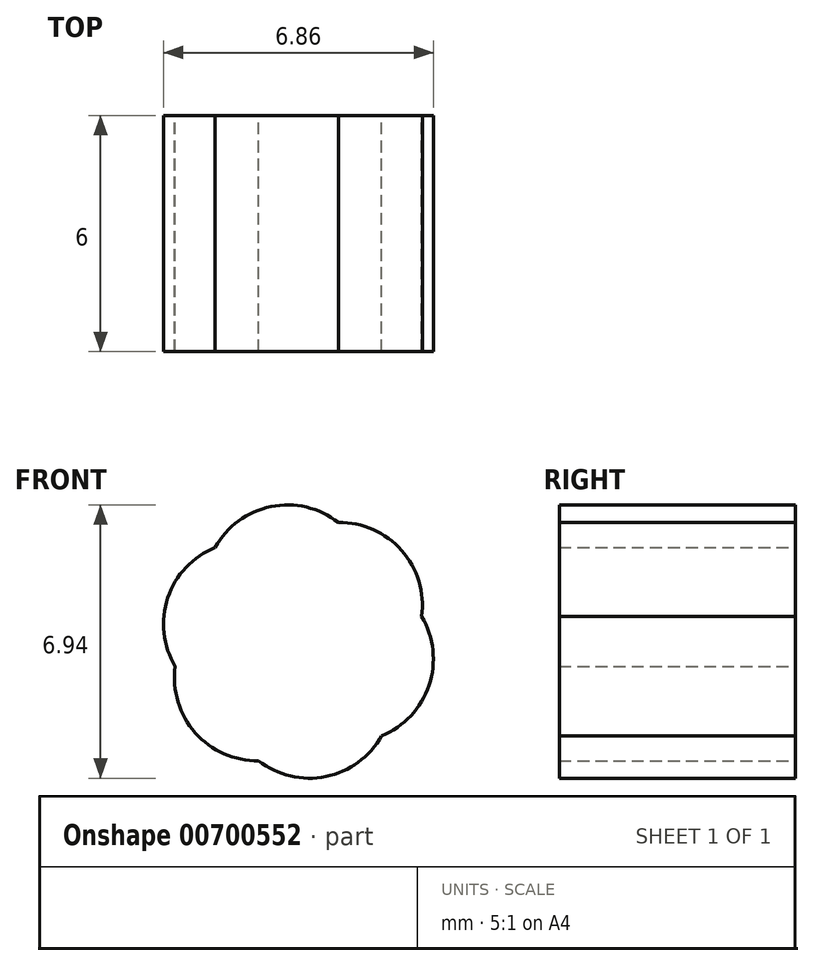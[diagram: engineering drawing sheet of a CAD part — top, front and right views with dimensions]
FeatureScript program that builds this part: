
annotation { "Feature Type Name" : "Feature", "Feature Type Description" : "" }
export const myFeature = defineFeature(function(context is Context, id is Id, definition is map)
    precondition{}
    {
        {
            var Q0;
            Q0=qCreatedBy(makeId("Front.planeOp"),FACE);
            var sketch = newSketch(context, id + "F0", { "sketchPlane" : qUnion([Q0])});
            skArc(sketch, "E0", {"start": v(3.13, 0.64) * mm, "mid": v(2.62, 2.32) * mm, "end": v(1.01, 3.03) * mm});
            skArc(sketch, "E1", {"start": v(2.11, -2.4) * mm, "mid": v(3.32, -1.11) * mm, "end": v(3.13, 0.64) * mm});
            skArc(sketch, "E2", {"start": v(-1.01, -3.03) * mm, "mid": v(0.7, -3.43) * mm, "end": v(2.11, -2.4) * mm});
            skArc(sketch, "E3", {"start": v(-3.13, -0.64) * mm, "mid": v(-2.62, -2.32) * mm, "end": v(-1.01, -3.03) * mm});
            skArc(sketch, "E4.trimOffspring", {"start": v(1.01, 3.03) * mm, "mid": v(-0.7, 3.43) * mm, "end": v(-2.11, 2.4) * mm});
            skArc(sketch, "E5.trimOffspring", {"start": v(-2.11, 2.4) * mm, "mid": v(-3.32, 1.11) * mm, "end": v(-3.13, -0.64) * mm});
            skSolve(sketch);
        }
        {
            var Q0;
            Q0 = qSketchRegion(id + "F0", true);
            extrude(context, id + "F1", {"entities" : qUnion([Q0]), "depth" : 6 * mm, "offsetDistance" : 25 * mm});
        }
    });
